# Revit family: TSM Multiground
name_source: partatom
category: HLS-Bauteile
units: mm (PartAtom-declared; Revit-internal decimal feet)

## family parameters
Arbeitsebenenbasiert = Ja
Beim Laden mit Abzugskörper schneiden = Nein
Bemaßung runder Anschluss = Durchmesser verwenden
Beschriftungsausrichtung beibehalten = Nein
Gemeinsam genutzt = Ja
Immer vertikal = Nein
Klassifizierung = Keine
Raumberechnungspunkt = Nein
Teiletyp = Normal

## types (2) — shared parameters
Fabrikat = MEFA
Kurztext1 = TSM Multiground
Kurztext2 = L= 40 mm
Länge = 40 mm  [stored 0.131234 ft]
Länge Innengewinde 1 = 10 mm
Material = Stahl
Mengeneinheit = St
Vorgabe-Ansicht = 1219 mm
min. Bohrlochtiefe = 50 mm
vpe = 100

## per-type parameters (varying)
| type | Artikelnummer | Bohrerdurchmesser | Gewicht | Gewicht pro Bauteil | Innengewinde | TSM Multiground |
| TSM Multiground, 10x 40, M8 x 10, TX55 | 2235650 | 10 mm | 0,02 kg | 0,02 kg | M8 | TSM Multiground 10 SeKo VZ55 IG M8 |
| TSM Multiground, 12x 40, M10 x 10, TX60 | 2235651 | 12 mm | 0,03 kg | 0,03 kg | M10 | TSM Multiground 12 SeKo VZ60 IG M10 |

note: [stored X ft] marks values corroborated as IEEE doubles in the binary element streams (Revit-internal decimal feet)
